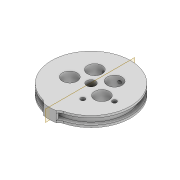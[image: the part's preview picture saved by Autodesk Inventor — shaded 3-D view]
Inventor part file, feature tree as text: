
AUTODESK INVENTOR PART (.ipt)
format: ipt  version: 2022 (Build 260153000, 153)  size: 281,088 bytes
history: native  units: mm
features: extrude x8, sketch x7, plane x3, fillet x2, pattern_circular x1, mirror x1, projected_geometry x1
ambient origin geometry x8: Origin, YZ Plane, XZ Plane, XY Plane, X Axis, Y Axis, Z Axis, Center Point
bodies: Solid1 (feature_tree)
feature tree (23):
  extrude  "Extrusion1"  Depth=33.75mm
  extrude  "Extrusion2"  Depth=3.0mm TaperAngle=0.0deg
  pattern_circular  "Circular Pattern1"  Count=5 Angle=360.0deg
  plane  "Work Plane1"
  plane  "Work Plane2"
  extrude  "Extrusion3"  [1 undecoded]
  extrude  "Extrusion4"  Depth=5.0mm
  fillet  "Fillet1"  Radius=2.5mm
  plane  "Work Plane3"
  extrude  "Extrusion5"  Depth=5.0mm TaperAngle=0.0deg
  mirror  "Mirror1"
  sketch  "Sketch6"  dims[d13=9.599311mm d14=-9.599311mm]
  extrude  "Extrusion6"  Depth=5.0mm
  extrude  "Extrusion7"  Depth=5.0mm
  extrude  "Extrusion8"  Depth=5.0mm
  fillet  "Fillet2"  Radius=10.0mm
  sketch  "Sketch1"  dims[d0=4.2mm d2=33.75mm]
  sketch  "Sketch2"  dims[d3=4.0mm d4=3.0mm d5=0.0mm]
  sketch  "Sketch3"  dims[d6=7.0mm]
  sketch  "Sketch4"  dims[d7=8.0mm]
  sketch  "Sketch5"  dims[d8=10.0mm d9=0.0mm d10=50.0mm d11=360.0deg]
  projected_geometry  "Projected Loop1"
  sketch  "Sketch7"  dims[d15=1.5mm d16=1.5mm d17=2.5mm d18=5.0mm d19=0.0mm d20=1.5mm d21=1.5mm d22=2.5mm d23=10.0mm d24=0.0mm d25=1.0mm d26=37.4mm d27=1.0mm d28=0.0mm d29=2.1mm d30=13.0mm d31=1.9mm d32=2.1mm d33=8.4mm d35=5.0mm d36=0.0mm d37=100.0mm d38=0.0mm d39=4.5mm d40=3.0mm d41=3.0mm d42=1.0mm d43=5.0mm d44=0.0mm d45=3.0mm d46=10.0mm d47=0.0mm d48=5.0mm d49=0.0mm]
note: 1 required parameter value undecoded (feature->parameter linkage not recoverable at this tier; creation-order binding heuristic only, values carry confidence <= 0.55)
